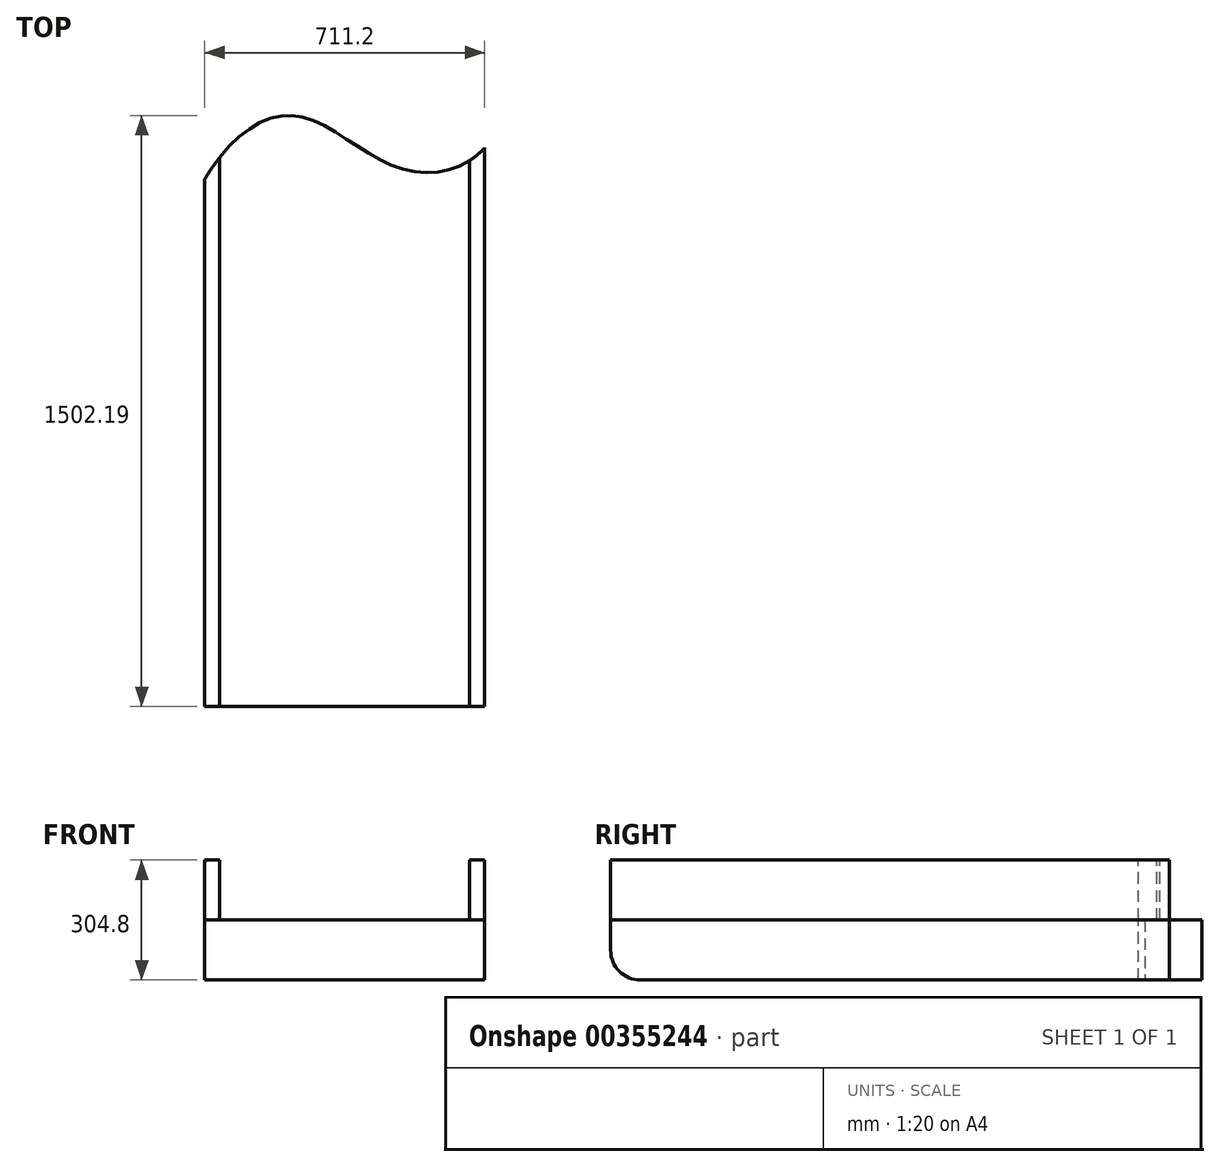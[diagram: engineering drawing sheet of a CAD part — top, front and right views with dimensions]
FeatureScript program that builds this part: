
annotation { "Feature Type Name" : "Feature", "Feature Type Description" : "" }
export const myFeature = defineFeature(function(context is Context, id is Id, definition is map)
    precondition{}
    {
        {
            var Q0;
            Q0=qCreatedBy(makeId("Front.planeOp"),FACE);
            var sketch = newSketch(context, id + "F0", { "sketchPlane" : qUnion([Q0])});
            skLineSegment(sketch, "E0.top", {"start": v(355.6, -76.2) * mm, "end": v(-355.6, -76.2) * mm});
            skLineSegment(sketch, "E0.left", {"start": v(355.6, 76.2) * mm, "end": v(355.6, -76.2) * mm});
            skLineSegment(sketch, "E0.right", {"start": v(-355.6, 76.2) * mm, "end": v(-355.6, -76.2) * mm});
            skPoint(sketch, "E0.middle", {"position": v(0, 0) * mm});
            skLineSegment(sketch, "E1.bottom", {"start": v(-355.6, -76.2) * mm, "end": v(355.6, -76.2) * mm});
            skLineSegment(sketch, "E1.top", {"start": v(-355.6, -228.6) * mm, "end": v(355.6, -228.6) * mm});
            skLineSegment(sketch, "E1.left", {"start": v(-355.6, -76.2) * mm, "end": v(-355.6, -228.6) * mm});
            skLineSegment(sketch, "E1.right", {"start": v(355.6, -76.2) * mm, "end": v(355.6, -228.6) * mm});
            skLineSegment(sketch, "E2", {"start": v(-355.6, 76.2) * mm, "end": v(-317.5, 76.2) * mm});
            skLineSegment(sketch, "E3", {"start": v(-317.5, 76.2) * mm, "end": v(-317.5, -76.2) * mm});
            skLineSegment(sketch, "E4", {"start": v(355.6, 76.2) * mm, "end": v(317.5, 76.2) * mm});
            skLineSegment(sketch, "E5", {"start": v(317.5, 76.2) * mm, "end": v(317.5, -76.2) * mm});
            skSolve(sketch);
        }
        {
            var Q0;
            Q0=makeQuery(id+"F0.imprint","IMPRINT",FACE,{"disambiguationData":[TD([[makeQuery(id+"F0.imprint","IMPRINT",EDGE,{"derivedFrom":sQuery(id+"F0.wireOp",EDGE,"E1.top")}),1.0]])]});
            extrude(context, id + "F1", {"entities" : qUnion([Q0]), "oppositeDirection" : true, "depth" : 3657.6 * mm});
        }
        {
            var Q0;
            {var subQ0=sQuery(id+"F0.wireOp",EDGE,"E0.right");Q0=makeQuery(id+"F0.imprint","IMPRINT",FACE,{"disambiguationData":[TD([[makeQuery(id+"F0.imprint","IMPRINT",EDGE,{"derivedFrom":subQ0}),1.0]])]});}
            var Q1;
            {var subQ0=sQuery(id+"F0.wireOp",EDGE,"E0.left");Q1=makeQuery(id+"F0.imprint","IMPRINT",FACE,{"disambiguationData":[TD([[makeQuery(id+"F0.imprint","IMPRINT",EDGE,{"derivedFrom":subQ0}),-1.0]])]});}
            extrude(context, id + "F2", {"entities" : qUnion([Q0, Q1]), "oppositeDirection" : true, "depth" : 3657.6 * mm});
        }
        {
            var Q0;
            Q0=makeQuery(id+"F1.opExtrude","CAP_EDGE",EDGE,{"disambiguationData":[OSD([sQuery(id+"F0.wireOp",EDGE,"E1.bottom")])],"isStart":true});
            var Q1;
            Q1=makeQuery(id+"F1.opExtrude","CAP_EDGE",EDGE,{"disambiguationData":[OSD([sQuery(id+"F0.wireOp",EDGE,"E1.top")])],"isStart":true});
            var Q2;
            Q2=makeQuery(id+"F1.opExtrude","CAP_EDGE",EDGE,{"disambiguationData":[OSD([sQuery(id+"F0.wireOp",EDGE,"E1.bottom")])],"isStart":false});
            var Q3;
            Q3=makeQuery(id+"F1.opExtrude","CAP_EDGE",EDGE,{"disambiguationData":[OSD([sQuery(id+"F0.wireOp",EDGE,"E1.top")])],"isStart":false});
            fillet(context, id + "F3", {"entities" : qUnion([Q0, Q1, Q2, Q3]), "radius" : 76.2 * mm, "tangentPropagation" : true, "allowEdgeOverflow" : false});
        }
        {
            var Q0;
            Q0=makeQuery(id+"F2.opExtrude","SWEPT_FACE",FACE,{"disambiguationData":[OSD([sQuery(id+"F0.wireOp",EDGE,"E2")])]});
            var sketch = newSketch(context, id + "F4", { "sketchPlane" : qUnion([Q0])});
            skFitSpline(sketch, "E6", {"points": [v(-355.6, 1340.72) * mm, v(-122.88, 1500.88) * mm, v(136.27, 1369.32) * mm, v(355.6, 1420) * mm], "startDerivative": vector(574.33, 938.6) * mm, "endDerivative": vector(528.56, 586.55) * mm});
            skFitSpline(sketch, "E7", {"points": [v(-355.6, 1340.72) * mm, v(-1214.09, 3517.19) * mm, v(46.71, 3757.84) * mm, v(690.2, 3731.68) * mm, v(355.6, 1420) * mm], "startDerivative": vector(-5480.8, 9981.81) * mm, "endDerivative": vector(-2618.72, -11092.62) * mm});
            skSolve(sketch);
        }
        {
            var Q0;
            {var subQ2=sQuery(id+"F4.wireOp",EDGE,"E7");Q0=makeQuery(id+"F4.imprint","IMPRINT",FACE,{"disambiguationData":[TD([[makeQuery(id+"F4.imprint","IMPRINT",EDGE,{"derivedFrom":subQ2}),-1.0]])]});}
            var Q1;
            {var subQ1=sQuery(id+"F0.wireOp",EDGE,"E2");var subQ6=makeQuery(id+"F2.opExtrude","CAP_EDGE",EDGE,{"disambiguationData":[OSD([subQ1])],"isStart":false});Q1=makeQuery(id+"F4.imprint","IMPRINT",FACE,{"disambiguationData":[TD([[makeQuery(id+"F4.imprint","IMPRINT",EDGE,{"derivedFrom":subQ6}),-1.0]])]});}
            extrude(context, id + "F5", {"entities" : qUnion([Q0, Q1]), "operationType" : NewBodyOperationType.REMOVE, "oppositeDirection" : true, "depth" : 457.2 * mm});
        }
    });
